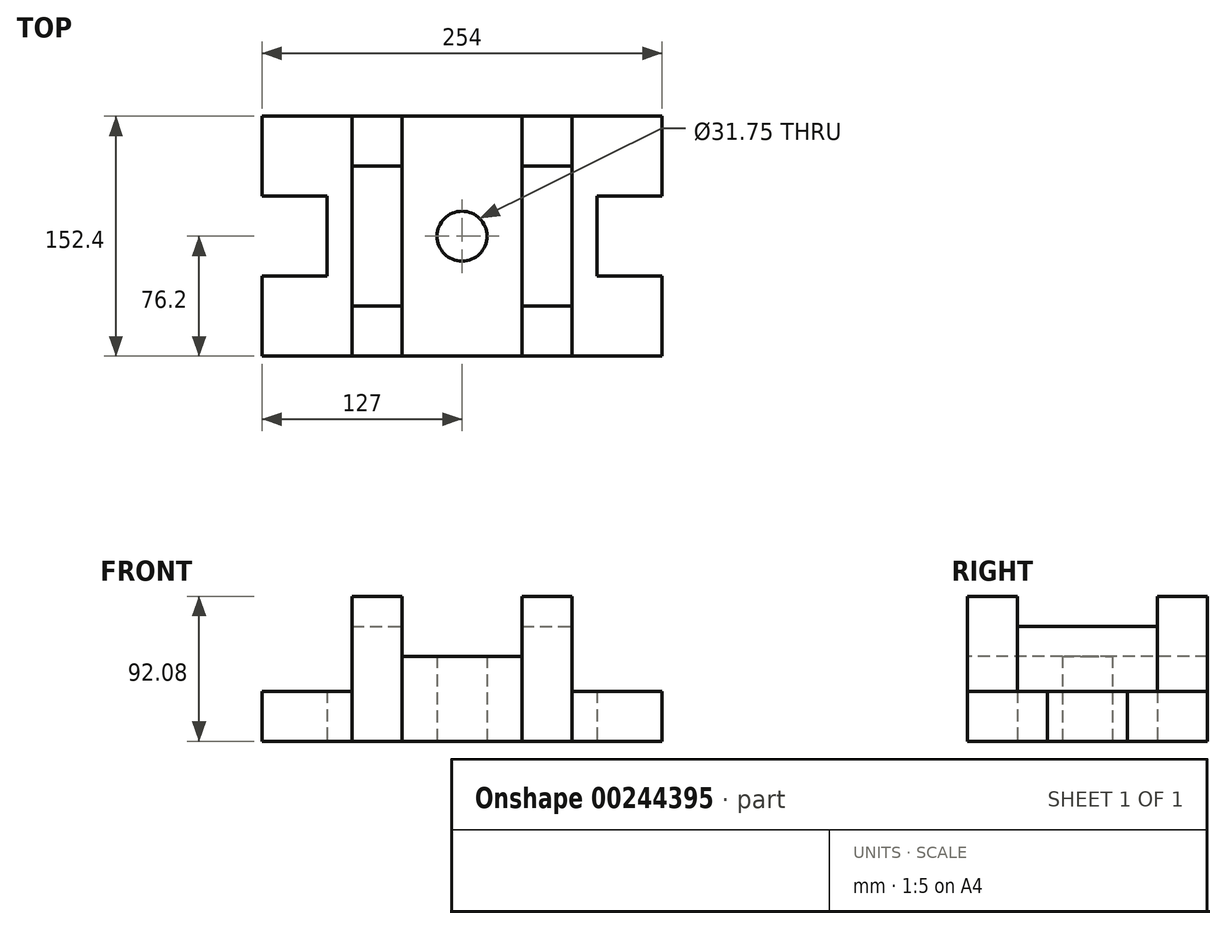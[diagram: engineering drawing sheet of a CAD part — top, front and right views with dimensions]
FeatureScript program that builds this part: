
annotation { "Feature Type Name" : "Feature", "Feature Type Description" : "" }
export const myFeature = defineFeature(function(context is Context, id is Id, definition is map)
    precondition{}
    {
        {
            var Q0;
            Q0=qCreatedBy(makeId("Top.planeOp"),FACE);
            var sketch = newSketch(context, id + "F0", { "sketchPlane" : qUnion([Q0])});
            skCircle(sketch, "E0", {"center": v(0, 0) * mm, "radius": 15.88 * mm});
            skLineSegment(sketch, "E1.bottom", {"start": v(-38.1, 76.2) * mm, "end": v(38.1, 76.2) * mm});
            skLineSegment(sketch, "E1.top", {"start": v(-38.1, -76.2) * mm, "end": v(38.1, -76.2) * mm});
            skLineSegment(sketch, "E1.left", {"start": v(-38.1, 76.2) * mm, "end": v(-38.1, -76.2) * mm});
            skLineSegment(sketch, "E1.right", {"start": v(38.1, 76.2) * mm, "end": v(38.1, -76.2) * mm});
            skLineSegment(sketch, "E2.bottom", {"start": v(-38.1, 76.2) * mm, "end": v(-69.85, 76.2) * mm});
            skLineSegment(sketch, "E2.top", {"start": v(-38.1, -76.2) * mm, "end": v(-69.85, -76.2) * mm});
            skLineSegment(sketch, "E2.right", {"start": v(-69.85, 76.2) * mm, "end": v(-69.85, -76.2) * mm});
            skLineSegment(sketch, "E3.bottom", {"start": v(38.1, 76.2) * mm, "end": v(69.85, 76.2) * mm});
            skLineSegment(sketch, "E3.top", {"start": v(38.1, -76.2) * mm, "end": v(69.85, -76.2) * mm});
            skLineSegment(sketch, "E3.right", {"start": v(69.85, 76.2) * mm, "end": v(69.85, -76.2) * mm});
            skLineSegment(sketch, "E4.bottom", {"start": v(-69.85, 76.2) * mm, "end": v(-127, 76.2) * mm});
            skLineSegment(sketch, "E4.top", {"start": v(-69.85, -76.2) * mm, "end": v(-127, -76.2) * mm});
            skLineSegment(sketch, "E4.right", {"start": v(-127, 76.2) * mm, "end": v(-127, 25.4) * mm});
            skLineSegment(sketch, "E5.bottom", {"start": v(69.85, 76.2) * mm, "end": v(127, 76.2) * mm});
            skLineSegment(sketch, "E5.top", {"start": v(69.85, -76.2) * mm, "end": v(127, -76.2) * mm});
            skLineSegment(sketch, "E5.right", {"start": v(127, 76.2) * mm, "end": v(127, 25.4) * mm});
            skLineSegment(sketch, "E6", {"start": v(-69.85, 44.45) * mm, "end": v(-38.1, 44.45) * mm});
            skLineSegment(sketch, "E7", {"start": v(-69.85, -44.45) * mm, "end": v(-38.1, -44.45) * mm});
            skLineSegment(sketch, "E8.trimOffspring", {"start": v(38.1, 44.45) * mm, "end": v(69.85, 44.45) * mm});
            skLineSegment(sketch, "E9.trimOffspring", {"start": v(38.1, -44.45) * mm, "end": v(69.85, -44.45) * mm});
            skLineSegment(sketch, "E10", {"start": v(-127, 25.4) * mm, "end": v(-85.73, 25.4) * mm});
            skLineSegment(sketch, "E11", {"start": v(-85.73, 25.4) * mm, "end": v(-85.72, -25.4) * mm});
            skLineSegment(sketch, "E12", {"start": v(-85.72, -25.4) * mm, "end": v(-127, -25.4) * mm});
            skLineSegment(sketch, "E13", {"start": v(127, 25.4) * mm, "end": v(85.72, 25.4) * mm});
            skLineSegment(sketch, "E14", {"start": v(85.72, 25.4) * mm, "end": v(85.72, -25.4) * mm});
            skLineSegment(sketch, "E15", {"start": v(85.72, -25.4) * mm, "end": v(127, -25.4) * mm});
            skLineSegment(sketch, "E16.trimOffspring", {"start": v(-127, -25.4) * mm, "end": v(-127, -76.2) * mm});
            skLineSegment(sketch, "E17.trimOffspring", {"start": v(127, -25.4) * mm, "end": v(127, -76.2) * mm});
            skSolve(sketch);
        }
        {
            var Q0;
            {var subQ3=sQuery(id+"F0.wireOp",EDGE,"E4.bottom");Q0=makeQuery(id+"F0.imprint","IMPRINT",FACE,{"disambiguationData":[TD([[makeQuery(id+"F0.imprint","IMPRINT",EDGE,{"derivedFrom":subQ3}),1.0]])]});}
            var Q1;
            {var subQ4=sQuery(id+"F0.wireOp",EDGE,"E5.bottom");Q1=makeQuery(id+"F0.imprint","IMPRINT",FACE,{"disambiguationData":[TD([[makeQuery(id+"F0.imprint","IMPRINT",EDGE,{"derivedFrom":subQ4}),-1.0]])]});}
            extrude(context, id + "F1", {"entities" : qUnion([Q0, Q1]), "depth" : 31.75 * mm});
        }
        {
            var Q0;
            {var subQ3=sQuery(id+"F0.wireOp",EDGE,"E4.bottom");Q0=makeQuery(id+"F0.imprint","IMPRINT",FACE,{"disambiguationData":[TD([[makeQuery(id+"F0.imprint","IMPRINT",EDGE,{"derivedFrom":subQ3}),1.0]])]});}
            var Q1;
            Q1=makeQuery(id+"F0.imprint","IMPRINT",FACE,{"disambiguationData":[TD([[makeQuery(id+"F0.imprint","IMPRINT",EDGE,{"derivedFrom":sQuery(id+"F0.wireOp",EDGE,"E0")}),-1.0]])]});
            extrude(context, id + "F2", {"entities" : qUnion([Q0, Q1]), "depth" : 53.97 * mm});
        }
        {
            var Q0;
            {var subQ0=sQuery(id+"F0.wireOp",EDGE,"E2.bottom");Q0=makeQuery(id+"F0.imprint","IMPRINT",FACE,{"disambiguationData":[TD([[makeQuery(id+"F0.imprint","IMPRINT",EDGE,{"derivedFrom":subQ0}),1.0]])]});}
            var Q1;
            {var subQ0=sQuery(id+"F0.wireOp",EDGE,"E2.top");Q1=makeQuery(id+"F0.imprint","IMPRINT",FACE,{"disambiguationData":[TD([[makeQuery(id+"F0.imprint","IMPRINT",EDGE,{"derivedFrom":subQ0}),-1.0]])]});}
            var Q2;
            {var subQ0=sQuery(id+"F0.wireOp",EDGE,"E3.top");Q2=makeQuery(id+"F0.imprint","IMPRINT",FACE,{"disambiguationData":[TD([[makeQuery(id+"F0.imprint","IMPRINT",EDGE,{"derivedFrom":subQ0}),1.0]])]});}
            var Q3;
            {var subQ0=sQuery(id+"F0.wireOp",EDGE,"E3.bottom");Q3=makeQuery(id+"F0.imprint","IMPRINT",FACE,{"disambiguationData":[TD([[makeQuery(id+"F0.imprint","IMPRINT",EDGE,{"derivedFrom":subQ0}),-1.0]])]});}
            extrude(context, id + "F3", {"entities" : qUnion([Q0, Q1, Q2, Q3]), "depth" : 92.07 * mm});
        }
        {
            var Q0;
            Q0=makeQuery(id+"F2.opExtrude","SWEPT_BODY",BODY,{"disambiguationData":[OSD([sQuery(id+"F0.wireOp",EDGE,"E4.bottom"),sQuery(id+"F0.wireOp",EDGE,"E4.top"),sQuery(id+"F0.wireOp",EDGE,"E2.right"),sQuery(id+"F0.wireOp",EDGE,"E4.right"),sQuery(id+"F0.wireOp",EDGE,"E10"),sQuery(id+"F0.wireOp",EDGE,"E11"),sQuery(id+"F0.wireOp",EDGE,"E12"),sQuery(id+"F0.wireOp",EDGE,"E16.trimOffspring")])]});
            deleteBodies(context, id + "F4", {"entities" : qUnion([Q0])});
        }
        {
            var Q0;
            Q0=makeQuery(id+"F0.imprint","IMPRINT",FACE,{"disambiguationData":[TD([[makeQuery(id+"F0.imprint","IMPRINT",EDGE,{"derivedFrom":sQuery(id+"F0.wireOp",EDGE,"E0")}),1.0]])]});
            extrude(context, id + "F5", {"entities" : qUnion([Q0]), "operationType" : NewBodyOperationType.REMOVE, "oppositeDirection" : true, "depth" : 31.75 * mm});
        }
        {
            var Q0;
            {var subQ0=sQuery(id+"F0.wireOp",EDGE,"E8.trimOffspring");Q0=makeQuery(id+"F0.imprint","IMPRINT",FACE,{"disambiguationData":[TD([[makeQuery(id+"F0.imprint","IMPRINT",EDGE,{"derivedFrom":subQ0}),-1.0]])]});}
            var Q1;
            {var subQ0=sQuery(id+"F0.wireOp",EDGE,"E6");Q1=makeQuery(id+"F0.imprint","IMPRINT",FACE,{"disambiguationData":[TD([[makeQuery(id+"F0.imprint","IMPRINT",EDGE,{"derivedFrom":subQ0}),-1.0]])]});}
            extrude(context, id + "F6", {"entities" : qUnion([Q0, Q1]), "depth" : 73.02 * mm});
        }
    });
